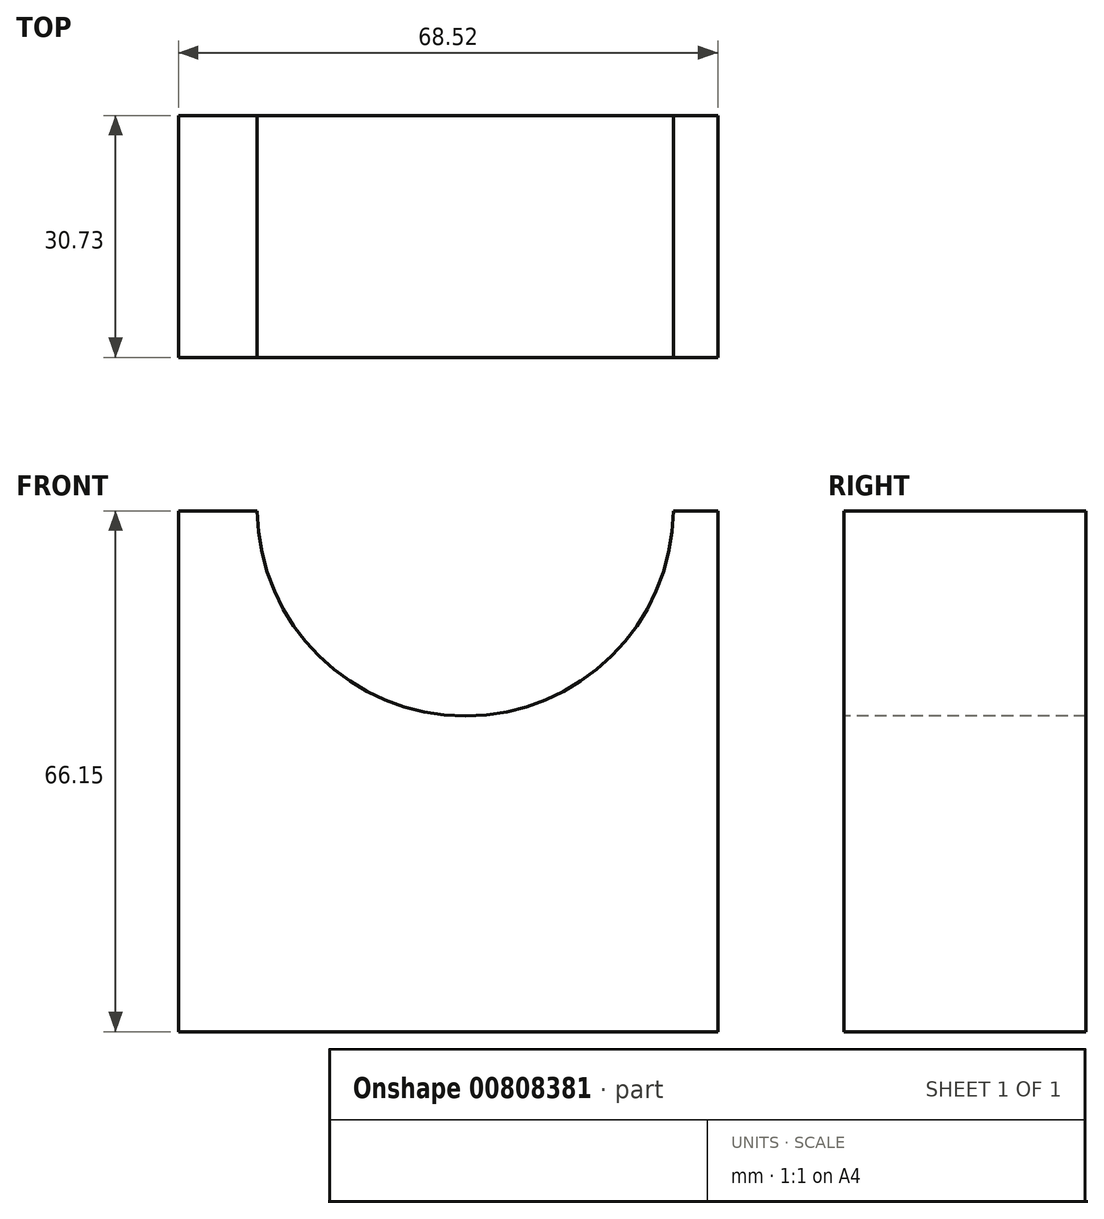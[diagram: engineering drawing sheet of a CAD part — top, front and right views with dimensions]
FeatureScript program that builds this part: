
annotation { "Feature Type Name" : "Feature", "Feature Type Description" : "" }
export const myFeature = defineFeature(function(context is Context, id is Id, definition is map)
    precondition{}
    {
        {
            var Q0;
            Q0=qCreatedBy(makeId("Front.planeOp"),FACE);
            var sketch = newSketch(context, id + "F0", { "sketchPlane" : qUnion([Q0])});
            skLineSegment(sketch, "E0", {"start": v(-36.44, 33.87) * mm, "end": v(41.2, 33.87) * mm});
            skLineSegment(sketch, "E1", {"start": v(41.2, 33.87) * mm, "end": v(41.2, -32.28) * mm});
            skLineSegment(sketch, "E2", {"start": v(-36.44, 33.87) * mm, "end": v(-36.44, -32.28) * mm});
            skLineSegment(sketch, "E3", {"start": v(-36.44, -32.28) * mm, "end": v(41.2, -32.28) * mm});
            skSolve(sketch);
        }
        {
            var Q0;
            Q0 = qSketchRegion(id + "F0", true);
            extrude(context, id + "F1", {"entities" : qUnion([Q0]), "oppositeDirection" : true, "depth" : 30.73 * mm, "offsetDistance" : 25.4 * mm});
        }
        {
            var Q0;
            Q0=qCreatedBy(makeId("Front.planeOp"),FACE);
            var sketch = newSketch(context, id + "F2", { "sketchPlane" : qUnion([Q0])});
            skCircle(sketch, "E4", {"center": v(0, 34.26) * mm, "radius": 26.44 * mm});
            skSolve(sketch);
        }
        {
            var Q0;
            Q0 = qSketchRegion(id + "F2", true);
            extrude(context, id + "F3", {"entities" : qUnion([Q0]), "operationType" : NewBodyOperationType.REMOVE, "oppositeDirection" : true, "depth" : 31.5 * mm, "offsetDistance" : 25.4 * mm});
        }
        {
            var Q0;
            Q0=qCreatedBy(makeId("Top.planeOp"),FACE);
            var sketch = newSketch(context, id + "F4", { "sketchPlane" : qUnion([Q0])});
            skLineSegment(sketch, "E5", {"start": v(32.08, 31.1) * mm, "end": v(32.08, 0) * mm});
            skLineSegment(sketch, "E6", {"start": v(32.08, 0) * mm, "end": v(41.59, 0) * mm});
            skLineSegment(sketch, "E7", {"start": v(41.59, 0) * mm, "end": v(41.59, 39.41) * mm});
            skLineSegment(sketch, "E8", {"start": v(41.59, 39.41) * mm, "end": v(32.08, 39.41) * mm});
            skLineSegment(sketch, "E9", {"start": v(32.08, 39.41) * mm, "end": v(32.08, 31.1) * mm});
            skSolve(sketch);
        }
        {
            var Q0;
            Q0 = qSketchRegion(id + "F4", true);
            extrude(context, id + "F5", {"entities" : qUnion([Q0]), "operationType" : NewBodyOperationType.REMOVE, "depth" : 78.49 * mm, "offsetDistance" : 25.4 * mm});
        }
        {
            var Q0;
            Q0 = qSketchRegion(id + "F4", true);
            extrude(context, id + "F6", {"entities" : qUnion([Q0]), "operationType" : NewBodyOperationType.REMOVE, "oppositeDirection" : true, "depth" : 70.36 * mm, "offsetDistance" : 25.4 * mm});
        }
    });
